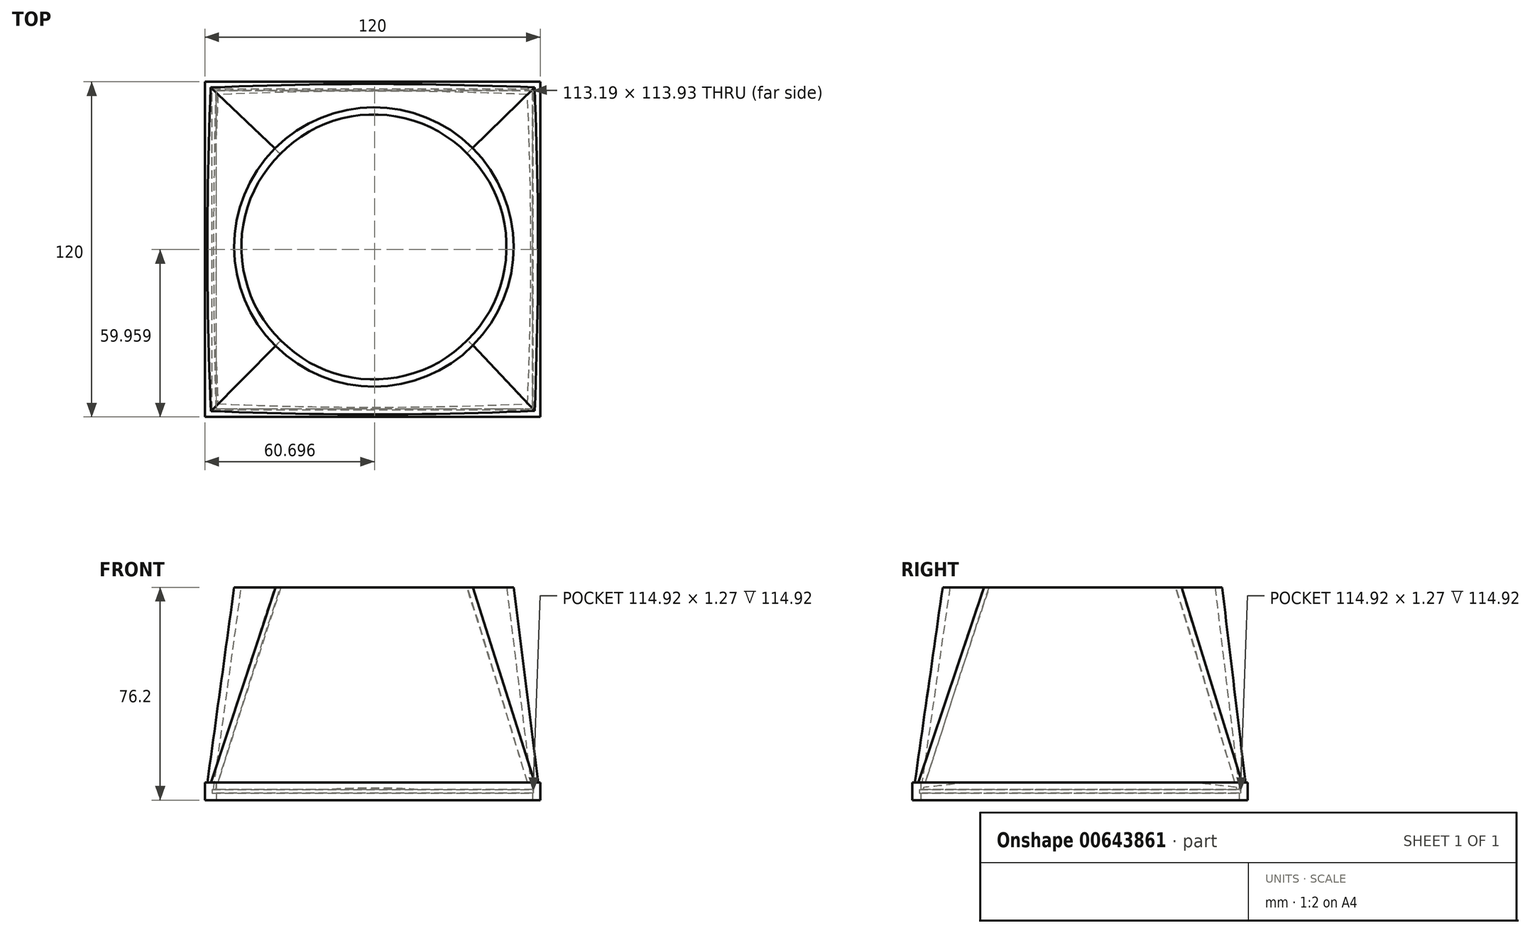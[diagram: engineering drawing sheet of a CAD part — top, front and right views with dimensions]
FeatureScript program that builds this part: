
annotation { "Feature Type Name" : "Feature", "Feature Type Description" : "" }
export const myFeature = defineFeature(function(context is Context, id is Id, definition is map)
    precondition{}
    {
        {
            var Q0;
            Q0=qCreatedBy(makeId("Top.planeOp"),FACE);
            var sketch = newSketch(context, id + "F0", { "sketchPlane" : qUnion([Q0])});
            skLineSegment(sketch, "E0.bottom", {"start": v(0, 0) * mm, "end": v(120, 0) * mm});
            skLineSegment(sketch, "E0.top", {"start": v(0, 120) * mm, "end": v(120, 120) * mm});
            skLineSegment(sketch, "E0.left", {"start": v(0, 0) * mm, "end": v(0, 120) * mm});
            skLineSegment(sketch, "E0.right", {"start": v(120, 0) * mm, "end": v(120, 120) * mm});
            skSolve(sketch);
        }
        {
            var Q0;
            Q0=makeQuery(id+"F0.imprint","IMPRINT",FACE,{"disambiguationData":[TD([[makeQuery(id+"F0.imprint","IMPRINT",EDGE,{"derivedFrom":sQuery(id+"F0.wireOp",EDGE,"E0.bottom")}),1.0]])]});
            extrude(context, id + "F1", {"entities" : qUnion([Q0]), "depth" : 6.35 * mm, "offsetDistance" : 25.4 * mm});
        }
        {
            var Q0;
            Q0=qCreatedBy(makeId("Top.planeOp"),FACE);
            cPlane(context, id + "F2", {"entities" : qUnion([Q0]), "cplaneType" : CPlaneType.OFFSET, "offset" : 76.2 * mm, "width" : 152.4 * mm, "height" : 152.4 * mm});
        }
        {
            var Q0;
            Q0=qCreatedBy(id+"F2.planeOp",FACE);
            var sketch = newSketch(context, id + "F3", { "sketchPlane" : qUnion([Q0])});
            skCircle(sketch, "E1", {"center": v(60.47, 60.88) * mm, "radius": 50 * mm});
            skSolve(sketch);
        }
        {
            var Q1;
            Q1=makeQuery(id+"F1.opExtrude","CAP_FACE",FACE,{"disambiguationData":[OSD([sQuery(id+"F0.wireOp",EDGE,"E0.bottom"),sQuery(id+"F0.wireOp",EDGE,"E0.top"),sQuery(id+"F0.wireOp",EDGE,"E0.left"),sQuery(id+"F0.wireOp",EDGE,"E0.right")])],"isStart":true});
            var Q2;
            Q2=makeQuery(id+"F3.imprint","IMPRINT",FACE,{"disambiguationData":[TD([[makeQuery(id+"F3.imprint","IMPRINT",EDGE,{"derivedFrom":sQuery(id+"F3.wireOp",EDGE,"E1")}),1.0]])]});
            loft(context, id + "F4", {"operationType" : NewBodyOperationType.ADD, "sheetProfilesArray" : [{ "sheetProfileEntities" : qUnion([Q1]) }, { "sheetProfileEntities" : qUnion([Q2]) }]});
        }
        {
            var Q0;
            Q0=makeQuery(id+"F4.opLoft","CAP_FACE",FACE,{"disambiguationData":[OSD([makeQuery(id+"F3.imprint","IMPRINT",FACE,{"disambiguationData":[TD([[makeQuery(id+"F3.imprint","IMPRINT",EDGE,{"derivedFrom":sQuery(id+"F3.wireOp",EDGE,"E1")}),1.0]])]})])],"isStart":true});
            shell(context, id + "F5", {"entities" : qUnion([Q0]), "thickness" : 2.54 * mm});
        }
        {
            var Q0;
            Q0=makeQuery(id+"F1.opExtrude","CAP_FACE",FACE,{"disambiguationData":[OSD([sQuery(id+"F0.wireOp",EDGE,"E0.bottom"),sQuery(id+"F0.wireOp",EDGE,"E0.top"),sQuery(id+"F0.wireOp",EDGE,"E0.left"),sQuery(id+"F0.wireOp",EDGE,"E0.right")])],"isStart":true});
            var sketch = newSketch(context, id + "F6", { "sketchPlane" : qUnion([Q0])});
            skLineSegment(sketch, "E2.bottom", {"start": v(4.1, -3) * mm, "end": v(117.3, -3) * mm});
            skLineSegment(sketch, "E2.top", {"start": v(4.1, -116.92) * mm, "end": v(117.3, -116.92) * mm});
            skLineSegment(sketch, "E2.left", {"start": v(4.1, -3) * mm, "end": v(4.1, -116.92) * mm});
            skLineSegment(sketch, "E2.right", {"start": v(117.3, -3) * mm, "end": v(117.3, -116.92) * mm});
            skSolve(sketch);
        }
        {
            var Q0;
            Q0=makeQuery(id+"F6.imprint","IMPRINT",FACE,{"disambiguationData":[TD([[makeQuery(id+"F6.imprint","IMPRINT",EDGE,{"derivedFrom":sQuery(id+"F6.wireOp",EDGE,"E2.bottom")}),-1.0]])]});
            extrude(context, id + "F7", {"entities" : qUnion([Q0]), "operationType" : NewBodyOperationType.REMOVE, "oppositeDirection" : true, "depth" : 6.35 * mm, "offsetDistance" : 25.4 * mm});
        }
    });
